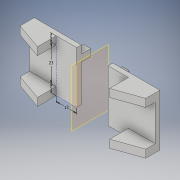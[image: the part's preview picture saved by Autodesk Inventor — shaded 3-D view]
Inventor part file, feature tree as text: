
AUTODESK INVENTOR PART (.ipt)
format: ipt  version: 2019 (Build 230136000, 136)  size: 151,040 bytes
history: native  units: mm
features: sketch x6, extrude x4, other x2, mirror x1
ambient origin geometry x8: Origin, YZ Plane, XZ Plane, XY Plane, X Axis, Y Axis, Z Axis, Center Point
bodies: Body1 (feature_tree)
feature tree (13):
  other  "Bryła1"
  sketch  "Szkic1"
  extrude  "Wyciągnięcie proste1"  Depth=4.5mm
  extrude  "Wyciągnięcie proste2"  Depth=4.5mm
  sketch  "Szkic4"
  extrude  "Wyciągnięcie proste3"  Depth=6.0mm TaperAngle=0.0deg
  extrude  "Wyciągnięcie proste4"  Depth=5.0mm
  other  "Płaszczyzna konstrukcyjna1"
  mirror  "Odbij1"
  sketch  "Szkic2"
  sketch  "Szkic3"
  sketch  "Szkic5"
  sketch  "Szkic6"
